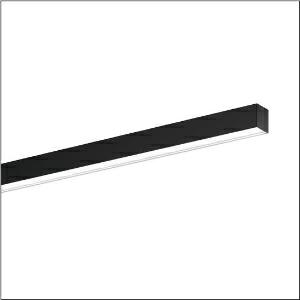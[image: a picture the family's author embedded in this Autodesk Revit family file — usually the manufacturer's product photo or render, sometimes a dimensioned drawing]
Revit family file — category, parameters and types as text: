
# Revit family: silica_r__21_51mx20da42bb_071f
name_source: partatom
category: Lighting Fixtures
units: mm (PartAtom-declared; Revit-internal decimal feet)

## family parameters
Cut with Voids When Loaded = No
Host = Face
Light Source = No
Part Type = Normal
Room Calculation Point = No
Round Connector Dimension = Use Diameter
Shared = No

## types (1)
- --- (1 x LED, 2400 lm, 15.2 W, 4000K)
    Apparent Load = 15 VA
    CIE Flux Codes = 48 79 96 100 100
    Color Rendering = 80
    Color Temperature = 4000K
    Default Elevation = 1800 mm
    Description = Silica® 21, office luminaire, primary optical cover: cover, of PMMA, opal, light emission: direct distribution, primary light characteristic: symmetric, installation type: surface-mounted, LED, rated luminous flux: 2.400lm, luminous efficacy: 158lm/W, light colour: 840, colour temperature: 4000K, with terminal, 3+2-pole, max. 2.5mm², mains connection: 220..240V, AC, 50/60Hz, rated input power: 15.2W, luminaire housing, of aluminium, jet black (RAL 9005), length: 1.204mm, width: 53mm, height: 53mm, protection rating (complete): IP20, insulation class (complete): insulation class I (protective earthing), certification: CE, permissible operating ambient temperature: 0..+35°C, standard: EN 50419, packaging unit: 1 piece
    Height = 0 mm  [stored 0 ft]
    Lamp = 1 x LED
    Lamp Light Flux = 2400 lm
    Lamp Power = 15.2 W
    Lamp count = 1
    Length = 1204 mm
    Luminous efficacy = 158 lm/W
    Manufacturer = Siteco
    ModVariant = No
    Model = 51MX20DA42BB
    Mounting Place = Ceiling
    Mounting Type = Recessed
    Number of Poles = 1
    OnlyDefault = Yes
    Power Factor = 1
    Product Name = Silica® 21
    Product group = office luminaire | ceiling recessed
    ProductGroupID = 401
    Protection Class = Protection class I
    Protection Degree = IP 20
    RLX_Detail_Level = 1
    RLX_Emergency_Light_Flux = 0 lm
    RLX_Emergency_Type = 0
    RLX_Emergency_Type_DB = No
    RlxData = <blob elided: 28705 chars, md5=33eabc48>
    Socket = socket
    Standby Power = 0 W
    System Light Flux = 2400 lm
    System Power = 15 W
    Type Comments = factory setting: luminous flux: 100 % | dim-lin: 254 | 218 mA
    Type Image = l_1297760.jpg
    URL = http://relux.com
    VarID = @adj_048369
    Voltage = 0 V
    Weight = 0.00 kg
    Width = 53 mm

note: [stored X ft] marks values corroborated as IEEE doubles in the binary element streams (Revit-internal decimal feet)

## geometry (parser evidence)
native form markers: Blend x4, Sweep x11
no freeform markers — native parametric forms only
